# Revit family: Universalkonsole mit Knoten 200x350x 4
name_source: partatom
category: HLS-Bauteile
revit_build: Autodesk Revit 2017 (Build: 20190507_1515(x64)
units: mm (PartAtom-declared; Revit-internal decimal feet)

## family parameters
Basisbauteil = Fläche
Beim Laden mit Abzugskörper schneiden = Nein
Bemaßung runder Anschluss = Durchmesser verwenden
Gemeinsam genutzt = Ja
Raumberechnungspunkt = Nein
Teiletyp = Normal

## types (1)
- Universalkonsole mit Knoten 200x350x 4
    Abmessung = 200 x 350 x 4 mm
    Artikelnummer = 081423501
    Ausführung = mit Streben
    EAN = 4250928419927
    Fabrikat = MEFA
    Firma = MEFA Befestigungs- und Montagesysteme GmbH
    Gewicht = 2.03 kg
    Gewicht pro Bauteil = 2.03 kg
    Höhe = 200 mm
    Kurztext1 = Universalkonsole mit 2 Streben
    Kurztext2 = 200 x 350 x 4 mm
    L1 = 200 mm
    L2 = 350 mm  [stored 1.14829 ft]
    Länge = 350 mm  [stored 1.14829 ft]
    Material = Stahl
    Materialname = S235
    Mengeneinheit = St
    Oberflaeche = galvanisch verzinkt
    Stärke = 4 mm  [stored 0.0131234 ft]
    Vorgabe-Ansicht = 1219 mm
    max. zul. Last F1 = 1.39 kip
    max. zul. Last F2 = 1.10 kip
    vpe = 10 St

note: [stored X ft] marks values corroborated as IEEE doubles in the binary element streams (Revit-internal decimal feet)
